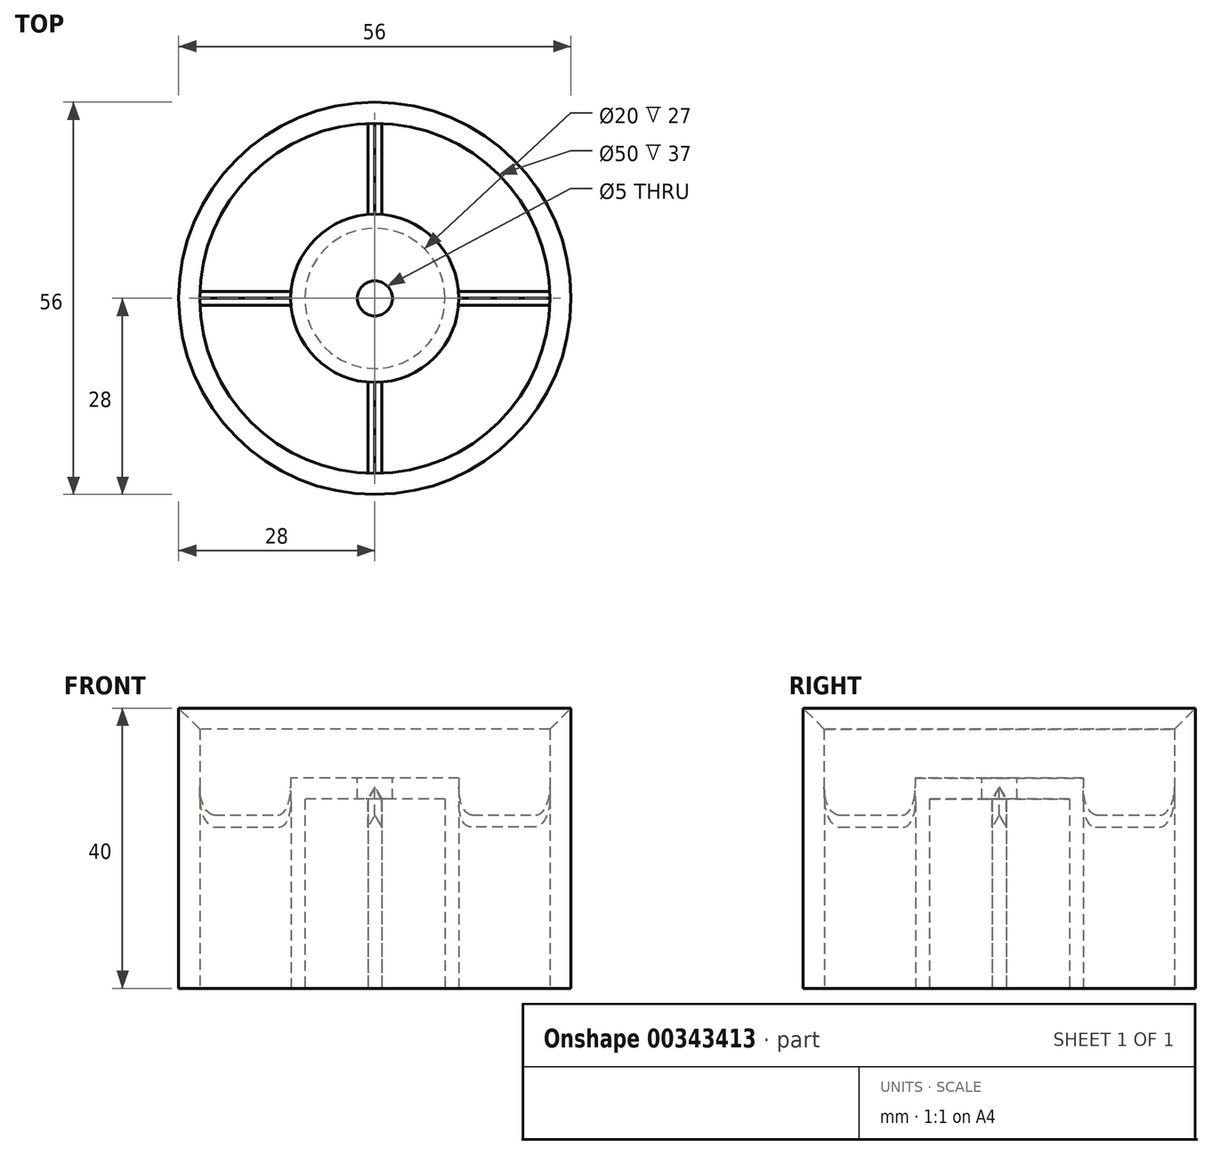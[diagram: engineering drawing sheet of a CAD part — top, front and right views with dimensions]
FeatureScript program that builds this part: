
annotation { "Feature Type Name" : "Feature", "Feature Type Description" : "" }
export const myFeature = defineFeature(function(context is Context, id is Id, definition is map)
    precondition{}
    {
        {
            var Q0;
            Q0=qCreatedBy(makeId("Top.planeOp"),FACE);
            var sketch = newSketch(context, id + "F0", { "sketchPlane" : qUnion([Q0])});
            skCircle(sketch, "E0", {"center": v(0, 0) * mm, "radius": 25 * mm});
            skCircle(sketch, "E1", {"center": v(0, 0) * mm, "radius": 28 * mm});
            skCircle(sketch, "E2", {"center": v(0, 0) * mm, "radius": 10 * mm});
            skCircle(sketch, "E3", {"center": v(0, 0) * mm, "radius": 12 * mm});
            skSolve(sketch);
        }
        {
            var Q0;
            Q0=makeQuery(id+"F0.imprint","IMPRINT",FACE,{"disambiguationData":[TD([[makeQuery(id+"F0.imprint","IMPRINT",EDGE,{"derivedFrom":sQuery(id+"F0.wireOp",EDGE,"E0")}),-1.0]])]});
            extrude(context, id + "F1", {"entities" : qUnion([Q0]), "depth" : 40 * mm});
        }
        {
            var Q0;
            Q0=makeQuery(id+"F0.imprint","IMPRINT",FACE,{"disambiguationData":[TD([[makeQuery(id+"F0.imprint","IMPRINT",EDGE,{"derivedFrom":sQuery(id+"F0.wireOp",EDGE,"E2")}),-1.0]])]});
            extrude(context, id + "F2", {"entities" : qUnion([Q0]), "depth" : 30 * mm});
        }
        {
            var Q0;
            Q0=qCreatedBy(makeId("Top.planeOp"),FACE);
            var sketch = newSketch(context, id + "F3", { "sketchPlane" : qUnion([Q0])});
            skArc(sketch, "E4.0", {"start": v(1, 24.98) * mm, "mid": v(0, 25) * mm, "end": v(-1, 24.98) * mm});
            skArc(sketch, "E4.1", {"start": v(1, 11.96) * mm, "mid": v(0, 12) * mm, "end": v(-1, 11.96) * mm});
            skLineSegment(sketch, "E5", {"start": v(-1, 11.96) * mm, "end": v(-1, 24.98) * mm});
            skLineSegment(sketch, "E6", {"start": v(1, 24.98) * mm, "end": v(1, 11.96) * mm});
            skArc(sketch, "E7.1.0", {"start": v(-24.98, 1) * mm, "mid": v(-25, 0) * mm, "end": v(-24.98, -1) * mm});
            skLineSegment(sketch, "E7.1.1", {"start": v(-24.98, 1) * mm, "end": v(-11.96, 1) * mm});
            skArc(sketch, "E7.1.2", {"start": v(-11.96, 1) * mm, "mid": v(-12, 0) * mm, "end": v(-11.96, -1) * mm});
            skLineSegment(sketch, "E7.1.3", {"start": v(-11.96, -1) * mm, "end": v(-24.98, -1) * mm});
            skArc(sketch, "E7.2.0", {"start": v(-1, -24.98) * mm, "mid": v(0, -25) * mm, "end": v(1, -24.98) * mm});
            skLineSegment(sketch, "E7.2.1", {"start": v(-1, -24.98) * mm, "end": v(-1, -11.96) * mm});
            skArc(sketch, "E7.2.2", {"start": v(-1, -11.96) * mm, "mid": v(0, -12) * mm, "end": v(1, -11.96) * mm});
            skLineSegment(sketch, "E7.2.3", {"start": v(1, -11.96) * mm, "end": v(1, -24.98) * mm});
            skLineSegment(sketch, "E8.4.3.0", {"start": v(24.98, -1) * mm, "end": v(11.96, -1) * mm});
            skArc(sketch, "E8.7.3.0", {"start": v(11.96, -1) * mm, "mid": v(12, 0) * mm, "end": v(11.96, 1) * mm});
            skArc(sketch, "E8.10.3.0", {"start": v(24.98, -1) * mm, "mid": v(25, 0) * mm, "end": v(24.98, 1) * mm});
            skLineSegment(sketch, "E8.11.3.0", {"start": v(11.96, 1) * mm, "end": v(24.98, 1) * mm});
            skSolve(sketch);
        }
        {
            var Q0;
            Q0 = qSketchRegion(id + "F3", true);
            extrude(context, id + "F4", {"entities" : qUnion([Q0]), "operationType" : NewBodyOperationType.ADD, "depth" : 25 * mm});
        }
        {
            var Q0;
            Q0=makeQuery(id+"F1.opExtrude","CAP_EDGE",EDGE,{"disambiguationData":[OSD([sQuery(id+"F0.wireOp",EDGE,"E0")])],"isStart":false});
            chamfer(context, id + "F5", {"entities" : qUnion([Q0]), "chamferType" : ChamferType.OFFSET_ANGLE, "width" : 3 * mm, "oppositeDirection" : false, "angle" : 45 * degree, "tangentPropagation" : true});
        }
        {
            var Q0;
            Q0=makeQuery(id+"F4.opExtrude","CAP_EDGE",EDGE,{"disambiguationData":[OSD([sQuery(id+"F3.wireOp",EDGE,"E7.1.3")])],"isStart":false});
            var Q1;
            Q1=makeQuery(id+"F4.opExtrude","CAP_EDGE",EDGE,{"disambiguationData":[OSD([sQuery(id+"F3.wireOp",EDGE,"E7.1.1")])],"isStart":false});
            var Q2;
            Q2=makeQuery(id+"F4.opExtrude","CAP_EDGE",EDGE,{"disambiguationData":[OSD([sQuery(id+"F3.wireOp",EDGE,"E6")])],"isStart":false});
            var Q3;
            Q3=makeQuery(id+"F4.opExtrude","CAP_EDGE",EDGE,{"disambiguationData":[OSD([sQuery(id+"F3.wireOp",EDGE,"E5")])],"isStart":false});
            var Q4;
            Q4=makeQuery(id+"F4.opExtrude","CAP_EDGE",EDGE,{"disambiguationData":[OSD([sQuery(id+"F3.wireOp",EDGE,"E8.4.3.0")])],"isStart":false});
            var Q5;
            Q5=makeQuery(id+"F4.opExtrude","CAP_EDGE",EDGE,{"disambiguationData":[OSD([sQuery(id+"F3.wireOp",EDGE,"E8.11.3.0")])],"isStart":false});
            var Q6;
            Q6=makeQuery(id+"F4.opExtrude","CAP_EDGE",EDGE,{"disambiguationData":[OSD([sQuery(id+"F3.wireOp",EDGE,"E7.2.3")])],"isStart":false});
            var Q7;
            Q7=makeQuery(id+"F4.opExtrude","CAP_EDGE",EDGE,{"disambiguationData":[OSD([sQuery(id+"F3.wireOp",EDGE,"E7.2.1")])],"isStart":false});
            chamfer(context, id + "F6", {"entities" : qUnion([Q0, Q1, Q2, Q3, Q4, Q5, Q6, Q7]), "chamferType" : ChamferType.OFFSET_ANGLE, "width" : 2 * mm, "oppositeDirection" : false, "angle" : 30 * degree, "tangentPropagation" : true});
        }
        {
            var Q0;
            Q0=makeQuery(id+"F4.opExtrude","SWEPT_EDGE",EDGE,{"disambiguationData":[OSD([sQuery(id+"F3.wireOp",EDGE,"E7.1.0"),sQuery(id+"F3.wireOp",EDGE,"E7.1.3")])]});
            var Q1;
            Q1=makeQuery(id+"F4.opExtrude","SWEPT_EDGE",EDGE,{"disambiguationData":[OSD([sQuery(id+"F3.wireOp",EDGE,"E7.2.2"),sQuery(id+"F3.wireOp",EDGE,"E7.2.3")])]});
            var Q2;
            Q2=makeQuery(id+"F4.opExtrude","SWEPT_EDGE",EDGE,{"disambiguationData":[OSD([sQuery(id+"F3.wireOp",EDGE,"E8.4.3.0"),sQuery(id+"F3.wireOp",EDGE,"E8.7.3.0")])]});
            var Q3;
            Q3=makeQuery(id+"F4.opExtrude","SWEPT_EDGE",EDGE,{"disambiguationData":[OSD([sQuery(id+"F3.wireOp",EDGE,"E7.2.1"),sQuery(id+"F3.wireOp",EDGE,"E7.2.2")])]});
            var Q4;
            Q4=makeQuery(id+"F4.opExtrude","SWEPT_EDGE",EDGE,{"disambiguationData":[OSD([sQuery(id+"F3.wireOp",EDGE,"E7.1.2"),sQuery(id+"F3.wireOp",EDGE,"E7.1.3")])]});
            var Q5;
            Q5=makeQuery(id+"F6.opChamfer","BLEND_EDGE",EDGE,{"blendedFrom":[makeQuery(id+"F4.opExtrude","CAP_EDGE",EDGE,{"disambiguationData":[OSD([sQuery(id+"F3.wireOp",EDGE,"E8.4.3.0")])],"isStart":false}),makeQuery(id+"F2.opExtrude","SWEPT_FACE",FACE,{"disambiguationData":[OSD([sQuery(id+"F0.wireOp",EDGE,"E3")])]})],"blendedInto":[makeQuery(id+"F2.opExtrude","SWEPT_FACE",FACE,{"disambiguationData":[OSD([sQuery(id+"F0.wireOp",EDGE,"E3")])]})]});
            var Q6;
            Q6=makeQuery(id+"F6.opChamfer","BLEND_EDGE",EDGE,{"blendedFrom":[makeQuery(id+"F4.opExtrude","CAP_EDGE",EDGE,{"disambiguationData":[OSD([sQuery(id+"F3.wireOp",EDGE,"E8.11.3.0")])],"isStart":false}),makeQuery(id+"F2.opExtrude","SWEPT_FACE",FACE,{"disambiguationData":[OSD([sQuery(id+"F0.wireOp",EDGE,"E3")])]})],"blendedInto":[makeQuery(id+"F2.opExtrude","SWEPT_FACE",FACE,{"disambiguationData":[OSD([sQuery(id+"F0.wireOp",EDGE,"E3")])]})]});
            var Q7;
            Q7=makeQuery(id+"F6.opChamfer","BLEND_EDGE",EDGE,{"blendedFrom":[makeQuery(id+"F4.opExtrude","CAP_EDGE",EDGE,{"disambiguationData":[OSD([sQuery(id+"F3.wireOp",EDGE,"E7.2.3")])],"isStart":false}),makeQuery(id+"F2.opExtrude","SWEPT_FACE",FACE,{"disambiguationData":[OSD([sQuery(id+"F0.wireOp",EDGE,"E3")])]})],"blendedInto":[makeQuery(id+"F2.opExtrude","SWEPT_FACE",FACE,{"disambiguationData":[OSD([sQuery(id+"F0.wireOp",EDGE,"E3")])]})]});
            var Q8;
            Q8=makeQuery(id+"F6.opChamfer","BLEND_EDGE",EDGE,{"blendedFrom":[makeQuery(id+"F4.opExtrude","CAP_EDGE",EDGE,{"disambiguationData":[OSD([sQuery(id+"F3.wireOp",EDGE,"E7.2.1")])],"isStart":false}),makeQuery(id+"F2.opExtrude","SWEPT_FACE",FACE,{"disambiguationData":[OSD([sQuery(id+"F0.wireOp",EDGE,"E3")])]})],"blendedInto":[makeQuery(id+"F2.opExtrude","SWEPT_FACE",FACE,{"disambiguationData":[OSD([sQuery(id+"F0.wireOp",EDGE,"E3")])]})]});
            var Q9;
            Q9=makeQuery(id+"F6.opChamfer","BLEND_EDGE",EDGE,{"blendedFrom":[makeQuery(id+"F4.opExtrude","CAP_EDGE",EDGE,{"disambiguationData":[OSD([sQuery(id+"F3.wireOp",EDGE,"E7.1.3")])],"isStart":false}),makeQuery(id+"F2.opExtrude","SWEPT_FACE",FACE,{"disambiguationData":[OSD([sQuery(id+"F0.wireOp",EDGE,"E3")])]})],"blendedInto":[makeQuery(id+"F2.opExtrude","SWEPT_FACE",FACE,{"disambiguationData":[OSD([sQuery(id+"F0.wireOp",EDGE,"E3")])]})]});
            var Q10;
            Q10=makeQuery(id+"F6.opChamfer","BLEND_EDGE",EDGE,{"blendedFrom":[makeQuery(id+"F4.opExtrude","CAP_EDGE",EDGE,{"disambiguationData":[OSD([sQuery(id+"F3.wireOp",EDGE,"E7.1.1")])],"isStart":false}),makeQuery(id+"F2.opExtrude","SWEPT_FACE",FACE,{"disambiguationData":[OSD([sQuery(id+"F0.wireOp",EDGE,"E3")])]})],"blendedInto":[makeQuery(id+"F2.opExtrude","SWEPT_FACE",FACE,{"disambiguationData":[OSD([sQuery(id+"F0.wireOp",EDGE,"E3")])]})]});
            var Q11;
            Q11=makeQuery(id+"F4.opExtrude","SWEPT_EDGE",EDGE,{"disambiguationData":[OSD([sQuery(id+"F3.wireOp",EDGE,"E7.1.1"),sQuery(id+"F3.wireOp",EDGE,"E7.1.2")])]});
            var Q12;
            Q12=makeQuery(id+"F4.opExtrude","SWEPT_EDGE",EDGE,{"disambiguationData":[OSD([sQuery(id+"F3.wireOp",EDGE,"E4.1"),sQuery(id+"F3.wireOp",EDGE,"E5")])]});
            var Q13;
            Q13=makeQuery(id+"F6.opChamfer","BLEND_EDGE",EDGE,{"blendedFrom":[makeQuery(id+"F4.opExtrude","CAP_EDGE",EDGE,{"disambiguationData":[OSD([sQuery(id+"F3.wireOp",EDGE,"E5")])],"isStart":false}),makeQuery(id+"F2.opExtrude","SWEPT_FACE",FACE,{"disambiguationData":[OSD([sQuery(id+"F0.wireOp",EDGE,"E3")])]})],"blendedInto":[makeQuery(id+"F2.opExtrude","SWEPT_FACE",FACE,{"disambiguationData":[OSD([sQuery(id+"F0.wireOp",EDGE,"E3")])]})]});
            var Q14;
            Q14=makeQuery(id+"F6.opChamfer","BLEND_EDGE",EDGE,{"blendedFrom":[makeQuery(id+"F4.opExtrude","CAP_EDGE",EDGE,{"disambiguationData":[OSD([sQuery(id+"F3.wireOp",EDGE,"E6")])],"isStart":false}),makeQuery(id+"F2.opExtrude","SWEPT_FACE",FACE,{"disambiguationData":[OSD([sQuery(id+"F0.wireOp",EDGE,"E3")])]})],"blendedInto":[makeQuery(id+"F2.opExtrude","SWEPT_FACE",FACE,{"disambiguationData":[OSD([sQuery(id+"F0.wireOp",EDGE,"E3")])]})]});
            var Q15;
            Q15=makeQuery(id+"F4.opExtrude","SWEPT_EDGE",EDGE,{"disambiguationData":[OSD([sQuery(id+"F3.wireOp",EDGE,"E4.1"),sQuery(id+"F3.wireOp",EDGE,"E6")])]});
            var Q16;
            Q16=makeQuery(id+"F4.opExtrude","SWEPT_EDGE",EDGE,{"disambiguationData":[OSD([sQuery(id+"F3.wireOp",EDGE,"E7.1.0"),sQuery(id+"F3.wireOp",EDGE,"E7.1.1")])]});
            var Q17;
            Q17=makeQuery(id+"F6.opChamfer","BLEND_EDGE",EDGE,{"blendedFrom":[makeQuery(id+"F4.opExtrude","CAP_EDGE",EDGE,{"disambiguationData":[OSD([sQuery(id+"F3.wireOp",EDGE,"E7.1.1")])],"isStart":false}),makeQuery(id+"F1.opExtrude","SWEPT_FACE",FACE,{"disambiguationData":[OSD([sQuery(id+"F0.wireOp",EDGE,"E0")])]})],"blendedInto":[makeQuery(id+"F1.opExtrude","SWEPT_FACE",FACE,{"disambiguationData":[OSD([sQuery(id+"F0.wireOp",EDGE,"E0")])]})]});
            var Q18;
            Q18=makeQuery(id+"F6.opChamfer","BLEND_EDGE",EDGE,{"blendedFrom":[makeQuery(id+"F4.opExtrude","CAP_EDGE",EDGE,{"disambiguationData":[OSD([sQuery(id+"F3.wireOp",EDGE,"E7.1.3")])],"isStart":false}),makeQuery(id+"F1.opExtrude","SWEPT_FACE",FACE,{"disambiguationData":[OSD([sQuery(id+"F0.wireOp",EDGE,"E0")])]})],"blendedInto":[makeQuery(id+"F1.opExtrude","SWEPT_FACE",FACE,{"disambiguationData":[OSD([sQuery(id+"F0.wireOp",EDGE,"E0")])]})]});
            var Q19;
            Q19=makeQuery(id+"F4.opExtrude","SWEPT_EDGE",EDGE,{"disambiguationData":[OSD([sQuery(id+"F3.wireOp",EDGE,"E8.7.3.0"),sQuery(id+"F3.wireOp",EDGE,"E8.11.3.0")])]});
            var Q20;
            Q20=makeQuery(id+"F4.opExtrude","SWEPT_EDGE",EDGE,{"disambiguationData":[OSD([sQuery(id+"F3.wireOp",EDGE,"E4.0"),sQuery(id+"F3.wireOp",EDGE,"E5")])]});
            var Q21;
            Q21=makeQuery(id+"F6.opChamfer","BLEND_EDGE",EDGE,{"blendedFrom":[makeQuery(id+"F4.opExtrude","CAP_EDGE",EDGE,{"disambiguationData":[OSD([sQuery(id+"F3.wireOp",EDGE,"E5")])],"isStart":false}),makeQuery(id+"F1.opExtrude","SWEPT_FACE",FACE,{"disambiguationData":[OSD([sQuery(id+"F0.wireOp",EDGE,"E0")])]})],"blendedInto":[makeQuery(id+"F1.opExtrude","SWEPT_FACE",FACE,{"disambiguationData":[OSD([sQuery(id+"F0.wireOp",EDGE,"E0")])]})]});
            var Q22;
            Q22=makeQuery(id+"F6.opChamfer","BLEND_EDGE",EDGE,{"blendedFrom":[makeQuery(id+"F4.opExtrude","CAP_EDGE",EDGE,{"disambiguationData":[OSD([sQuery(id+"F3.wireOp",EDGE,"E6")])],"isStart":false}),makeQuery(id+"F1.opExtrude","SWEPT_FACE",FACE,{"disambiguationData":[OSD([sQuery(id+"F0.wireOp",EDGE,"E0")])]})],"blendedInto":[makeQuery(id+"F1.opExtrude","SWEPT_FACE",FACE,{"disambiguationData":[OSD([sQuery(id+"F0.wireOp",EDGE,"E0")])]})]});
            var Q23;
            Q23=makeQuery(id+"F6.opChamfer","BLEND_EDGE",EDGE,{"blendedFrom":[makeQuery(id+"F4.opExtrude","CAP_EDGE",EDGE,{"disambiguationData":[OSD([sQuery(id+"F3.wireOp",EDGE,"E8.4.3.0")])],"isStart":false}),makeQuery(id+"F1.opExtrude","SWEPT_FACE",FACE,{"disambiguationData":[OSD([sQuery(id+"F0.wireOp",EDGE,"E0")])]})],"blendedInto":[makeQuery(id+"F1.opExtrude","SWEPT_FACE",FACE,{"disambiguationData":[OSD([sQuery(id+"F0.wireOp",EDGE,"E0")])]})]});
            var Q24;
            Q24=makeQuery(id+"F4.opExtrude","SWEPT_EDGE",EDGE,{"disambiguationData":[OSD([sQuery(id+"F3.wireOp",EDGE,"E8.4.3.0"),sQuery(id+"F3.wireOp",EDGE,"E8.10.3.0")])]});
            var Q25;
            Q25=makeQuery(id+"F6.opChamfer","BLEND_EDGE",EDGE,{"blendedFrom":[makeQuery(id+"F4.opExtrude","CAP_EDGE",EDGE,{"disambiguationData":[OSD([sQuery(id+"F3.wireOp",EDGE,"E8.11.3.0")])],"isStart":false}),makeQuery(id+"F1.opExtrude","SWEPT_FACE",FACE,{"disambiguationData":[OSD([sQuery(id+"F0.wireOp",EDGE,"E0")])]})],"blendedInto":[makeQuery(id+"F1.opExtrude","SWEPT_FACE",FACE,{"disambiguationData":[OSD([sQuery(id+"F0.wireOp",EDGE,"E0")])]})]});
            var Q26;
            Q26=makeQuery(id+"F4.opExtrude","SWEPT_EDGE",EDGE,{"disambiguationData":[OSD([sQuery(id+"F3.wireOp",EDGE,"E4.0"),sQuery(id+"F3.wireOp",EDGE,"E6")])]});
            var Q27;
            Q27=makeQuery(id+"F4.opExtrude","SWEPT_EDGE",EDGE,{"disambiguationData":[OSD([sQuery(id+"F3.wireOp",EDGE,"E7.2.0"),sQuery(id+"F3.wireOp",EDGE,"E7.2.3")])]});
            var Q28;
            Q28=makeQuery(id+"F6.opChamfer","BLEND_EDGE",EDGE,{"blendedFrom":[makeQuery(id+"F4.opExtrude","CAP_EDGE",EDGE,{"disambiguationData":[OSD([sQuery(id+"F3.wireOp",EDGE,"E7.2.3")])],"isStart":false}),makeQuery(id+"F1.opExtrude","SWEPT_FACE",FACE,{"disambiguationData":[OSD([sQuery(id+"F0.wireOp",EDGE,"E0")])]})],"blendedInto":[makeQuery(id+"F1.opExtrude","SWEPT_FACE",FACE,{"disambiguationData":[OSD([sQuery(id+"F0.wireOp",EDGE,"E0")])]})]});
            var Q29;
            Q29=makeQuery(id+"F4.opExtrude","SWEPT_EDGE",EDGE,{"disambiguationData":[OSD([sQuery(id+"F3.wireOp",EDGE,"E7.2.0"),sQuery(id+"F3.wireOp",EDGE,"E7.2.1")])]});
            var Q30;
            Q30=makeQuery(id+"F6.opChamfer","BLEND_EDGE",EDGE,{"blendedFrom":[makeQuery(id+"F4.opExtrude","CAP_EDGE",EDGE,{"disambiguationData":[OSD([sQuery(id+"F3.wireOp",EDGE,"E7.2.1")])],"isStart":false}),makeQuery(id+"F1.opExtrude","SWEPT_FACE",FACE,{"disambiguationData":[OSD([sQuery(id+"F0.wireOp",EDGE,"E0")])]})],"blendedInto":[makeQuery(id+"F1.opExtrude","SWEPT_FACE",FACE,{"disambiguationData":[OSD([sQuery(id+"F0.wireOp",EDGE,"E0")])]})]});
            var Q31;
            Q31=makeQuery(id+"F4.opExtrude","SWEPT_EDGE",EDGE,{"disambiguationData":[OSD([sQuery(id+"F3.wireOp",EDGE,"E8.10.3.0"),sQuery(id+"F3.wireOp",EDGE,"E8.11.3.0")])]});
            fillet(context, id + "F7", {"entities" : qUnion([Q0, Q1, Q2, Q3, Q4, Q5, Q6, Q7, Q8, Q9, Q10, Q11, Q12, Q13, Q14, Q15, Q16, Q17, Q18, Q19, Q20, Q21, Q22, Q23, Q24, Q25, Q26, Q27, Q28, Q29, Q30, Q31]), "radius" : 2 * mm, "allowEdgeOverflow" : false});
        }
        {
            var Q0;
            Q0=makeQuery(id+"F2.opExtrude","CAP_FACE",FACE,{"disambiguationData":[OSD([sQuery(id+"F0.wireOp",EDGE,"E2"),sQuery(id+"F0.wireOp",EDGE,"E3")])],"isStart":false});
            var sketch = newSketch(context, id + "F8", { "sketchPlane" : qUnion([Q0])});
            skCircle(sketch, "E9.0", {"center": v(0, 0) * mm, "radius": 12 * mm});
            skCircle(sketch, "E10", {"center": v(0, 0) * mm, "radius": 2.5 * mm});
            skSolve(sketch);
        }
        {
            var Q0;
            Q0 = qSketchRegion(id + "F8", true);
            var Q1;
            Q1=sQuery(id+"F8.wireOp",EDGE,"E9.0");
            extrude(context, id + "F9", {"entities" : qUnion([Q0]), "operationType" : NewBodyOperationType.ADD, "surfaceEntities" : qUnion([Q1]), "oppositeDirection" : true, "depth" : 3 * mm});
        }
    });
